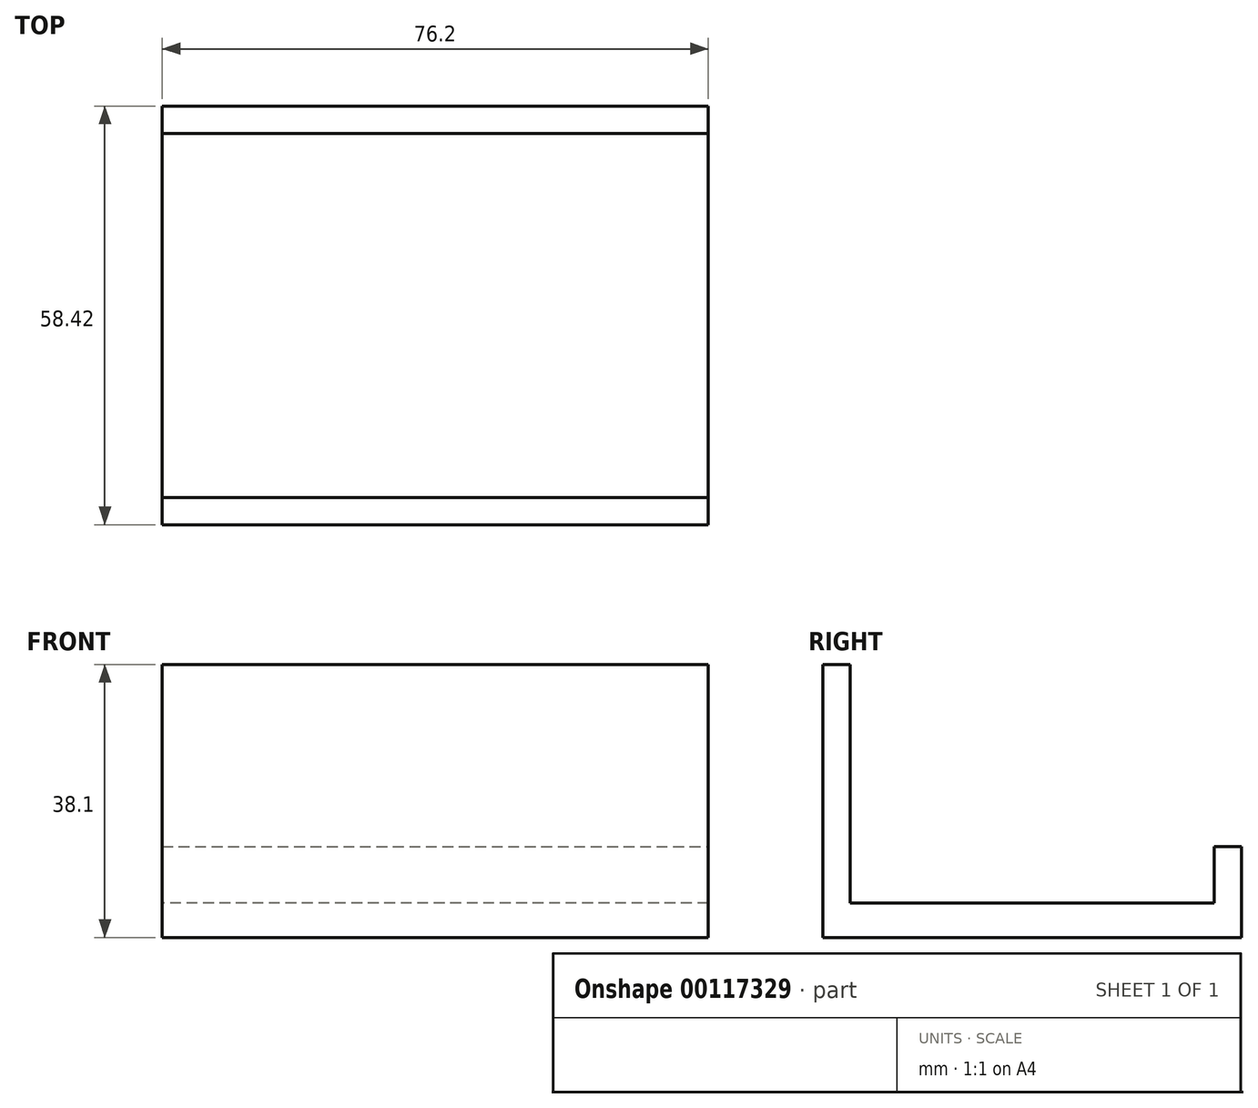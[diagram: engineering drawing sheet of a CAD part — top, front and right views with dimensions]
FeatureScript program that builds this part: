
annotation { "Feature Type Name" : "Feature", "Feature Type Description" : "" }
export const myFeature = defineFeature(function(context is Context, id is Id, definition is map)
    precondition{}
    {
        {
            var Q0;
            Q0=qCreatedBy(makeId("Top.planeOp"),FACE);
            var sketch = newSketch(context, id + "F0", { "sketchPlane" : qUnion([Q0])});
            skLineSegment(sketch, "E0.bottom", {"start": v(38.1, -25.4) * mm, "end": v(-38.1, -25.4) * mm});
            skLineSegment(sketch, "E0.top", {"start": v(38.1, 25.4) * mm, "end": v(-38.1, 25.4) * mm});
            skLineSegment(sketch, "E0.left", {"start": v(38.1, -25.4) * mm, "end": v(38.1, 25.4) * mm});
            skLineSegment(sketch, "E0.right", {"start": v(-38.1, -25.4) * mm, "end": v(-38.1, 25.4) * mm});
            skPoint(sketch, "E0.middle", {"position": v(0, 0) * mm});
            skSolve(sketch);
        }
        {
            var Q0;
            Q0=makeQuery(id+"F0.imprint","IMPRINT",FACE,{"disambiguationData":[TD([[makeQuery(id+"F0.imprint","IMPRINT",EDGE,{"derivedFrom":sQuery(id+"F0.wireOp",EDGE,"E0.bottom")}),-1.0]])]});
            var sketch = newSketch(context, id + "F1", { "sketchPlane" : qUnion([Q0])});
            skSolve(sketch);
        }
        {
            var Q0;
            Q0 = qSketchRegion(id + "F1", true);
            var Q1;
            Q1=makeQuery(id+"F0.imprint","IMPRINT",FACE,{"disambiguationData":[TD([[makeQuery(id+"F0.imprint","IMPRINT",EDGE,{"derivedFrom":sQuery(id+"F0.wireOp",EDGE,"E0.bottom")}),-1.0]])]});
            extrude(context, id + "F2", {"entities" : qUnion([Q0, Q1]), "depth" : 4.83 * mm});
        }
        {
            var Q0;
            Q0=makeQuery(id+"F2.opExtrude","SWEPT_FACE",FACE,{"disambiguationData":[OSD([sQuery(id+"F0.wireOp",EDGE,"E0.bottom")])]});
            var sketch = newSketch(context, id + "F3", { "sketchPlane" : qUnion([Q0])});
            skLineSegment(sketch, "E1.bottom", {"start": v(-38.1, 0) * mm, "end": v(38.1, 0) * mm});
            skLineSegment(sketch, "E1.top", {"start": v(-38.1, 38.1) * mm, "end": v(38.1, 38.1) * mm});
            skLineSegment(sketch, "E1.left", {"start": v(-38.1, 0) * mm, "end": v(-38.1, 38.1) * mm});
            skLineSegment(sketch, "E1.right", {"start": v(38.1, 0) * mm, "end": v(38.1, 38.1) * mm});
            skSolve(sketch);
        }
        {
            var Q0;
            Q0 = qSketchRegion(id + "F3", true);
            extrude(context, id + "F4", {"entities" : qUnion([Q0]), "operationType" : NewBodyOperationType.ADD, "depth" : 3.8 * mm});
        }
        {
            var Q0;
            Q0=makeQuery(id+"F2.opExtrude","SWEPT_FACE",FACE,{"disambiguationData":[OSD([sQuery(id+"F0.wireOp",EDGE,"E0.top")])]});
            var sketch = newSketch(context, id + "F5", { "sketchPlane" : qUnion([Q0])});
            skLineSegment(sketch, "E2.bottom", {"start": v(38.1, 0) * mm, "end": v(-38.1, 0) * mm});
            skLineSegment(sketch, "E2.top", {"start": v(38.1, 12.7) * mm, "end": v(-38.1, 12.7) * mm});
            skLineSegment(sketch, "E2.left", {"start": v(38.1, 0) * mm, "end": v(38.1, 12.7) * mm});
            skLineSegment(sketch, "E2.right", {"start": v(-38.1, 0) * mm, "end": v(-38.1, 12.7) * mm});
            skSolve(sketch);
        }
        {
            var Q0;
            Q0 = qSketchRegion(id + "F5", true);
            extrude(context, id + "F6", {"entities" : qUnion([Q0]), "operationType" : NewBodyOperationType.ADD, "depth" : 3.8 * mm});
        }
    });
